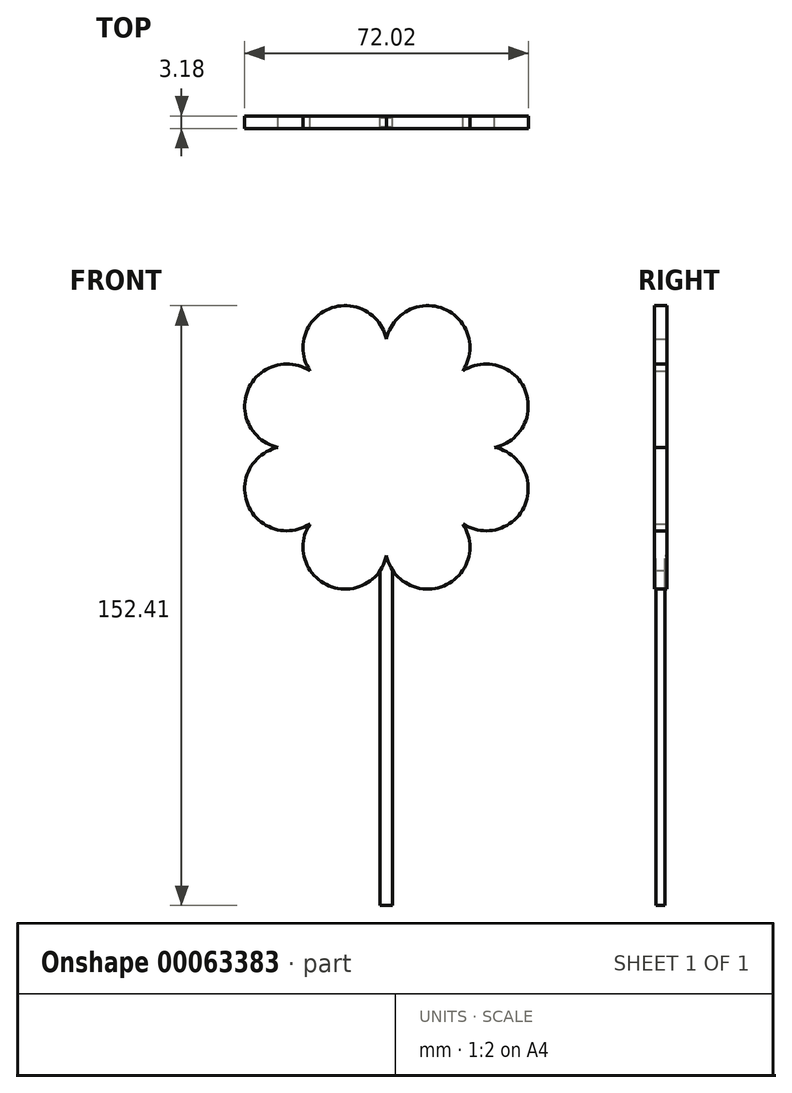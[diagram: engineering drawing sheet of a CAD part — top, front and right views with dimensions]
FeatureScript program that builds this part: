
annotation { "Feature Type Name" : "Feature", "Feature Type Description" : "" }
export const myFeature = defineFeature(function(context is Context, id is Id, definition is map)
    precondition{}
    {
        {
            var Q0;
            Q0=qCreatedBy(makeId("Front.planeOp"),FACE);
            var sketch = newSketch(context, id + "F0", { "sketchPlane" : qUnion([Q0])});
            skLineSegment(sketch, "E0", {"start": v(1.59, 0) * mm, "end": v(1.59, 88.9) * mm});
            skLineSegment(sketch, "E1", {"start": v(-1.59, 0) * mm, "end": v(-1.59, 88.9) * mm});
            skLineSegment(sketch, "E2", {"start": v(1.59, 0) * mm, "end": v(-1.59, 0) * mm});
            skCircle(sketch, "E3.cCircle", {"center": v(0, 116.4) * mm, "radius": 25.4 * mm, "construction": true});
            skLineSegment(sketch, "E3.0", {"start": v(-27.5, 116.4) * mm, "end": v(-19.44, 135.83) * mm});
            skLineSegment(sketch, "E3.1", {"start": v(-19.44, 135.83) * mm, "end": v(0, 143.89) * mm});
            skLineSegment(sketch, "E3.2", {"start": v(0, 143.89) * mm, "end": v(19.44, 135.83) * mm});
            skLineSegment(sketch, "E3.3", {"start": v(19.44, 135.83) * mm, "end": v(27.5, 116.4) * mm});
            skLineSegment(sketch, "E3.4", {"start": v(27.5, 116.4) * mm, "end": v(19.44, 96.95) * mm});
            skLineSegment(sketch, "E3.5", {"start": v(19.44, 96.95) * mm, "end": v(0, 88.9) * mm});
            skLineSegment(sketch, "E3.6", {"start": v(0, 88.9) * mm, "end": v(-19.44, 96.95) * mm});
            skLineSegment(sketch, "E3.7", {"start": v(-19.44, 96.95) * mm, "end": v(-27.5, 116.4) * mm});
            skPoint(sketch, "E3.0.midPoint", {"position": v(-23.47, 126.11) * mm});
            skLineSegment(sketch, "E4", {"start": v(1.59, 88.9) * mm, "end": v(-1.59, 88.9) * mm});
            skArc(sketch, "E5", {"start": v(-27.5, 116.4) * mm, "mid": v(-35.2, 101.81) * mm, "end": v(-19.44, 96.95) * mm});
            skArc(sketch, "E6", {"start": v(-19.44, 135.83) * mm, "mid": v(-35.2, 130.97) * mm, "end": v(-27.5, 116.4) * mm});
            skArc(sketch, "E7", {"start": v(0, 143.89) * mm, "mid": v(-14.58, 151.6) * mm, "end": v(-19.44, 135.83) * mm});
            skArc(sketch, "E8", {"start": v(19.44, 135.83) * mm, "mid": v(14.58, 151.6) * mm, "end": v(0, 143.89) * mm});
            skArc(sketch, "E9", {"start": v(27.5, 116.4) * mm, "mid": v(35.2, 130.97) * mm, "end": v(19.44, 135.83) * mm});
            skArc(sketch, "E10", {"start": v(19.44, 96.95) * mm, "mid": v(35.2, 101.81) * mm, "end": v(27.5, 116.4) * mm});
            skArc(sketch, "E11", {"start": v(0, 88.9) * mm, "mid": v(14.58, 81.2) * mm, "end": v(19.44, 96.95) * mm});
            skArc(sketch, "E12", {"start": v(-19.44, 96.95) * mm, "mid": v(-14.58, 81.2) * mm, "end": v(0, 88.9) * mm});
            skSolve(sketch);
        }
        {
            var Q0;
            Q0=makeQuery(id+"F0.imprint","IMPRINT",FACE,{"disambiguationData":[TD([[makeQuery(id+"F0.imprint","IMPRINT",EDGE,{"derivedFrom":sQuery(id+"F0.wireOp",EDGE,"E3.0")}),-1.0]])]});
            var Q1;
            {var subQ2=sQuery(id+"F0.wireOp",EDGE,"E3.5");Q1=makeQuery(id+"F0.imprint","IMPRINT",FACE,{"disambiguationData":[TD([[makeQuery(id+"F0.imprint","IMPRINT",EDGE,{"derivedFrom":subQ2}),1.0]])]});}
            var Q2;
            {var subQ0=sQuery(id+"F0.wireOp",EDGE,"E3.4");Q2=makeQuery(id+"F0.imprint","IMPRINT",FACE,{"disambiguationData":[TD([[makeQuery(id+"F0.imprint","IMPRINT",EDGE,{"derivedFrom":subQ0}),1.0]])]});}
            var Q3;
            {var subQ0=sQuery(id+"F0.wireOp",EDGE,"E3.3");Q3=makeQuery(id+"F0.imprint","IMPRINT",FACE,{"disambiguationData":[TD([[makeQuery(id+"F0.imprint","IMPRINT",EDGE,{"derivedFrom":subQ0}),1.0]])]});}
            var Q4;
            {var subQ0=sQuery(id+"F0.wireOp",EDGE,"E3.2");Q4=makeQuery(id+"F0.imprint","IMPRINT",FACE,{"disambiguationData":[TD([[makeQuery(id+"F0.imprint","IMPRINT",EDGE,{"derivedFrom":subQ0}),1.0]])]});}
            var Q5;
            {var subQ0=sQuery(id+"F0.wireOp",EDGE,"E3.1");Q5=makeQuery(id+"F0.imprint","IMPRINT",FACE,{"disambiguationData":[TD([[makeQuery(id+"F0.imprint","IMPRINT",EDGE,{"derivedFrom":subQ0}),1.0]])]});}
            var Q6;
            {var subQ0=sQuery(id+"F0.wireOp",EDGE,"E3.0");Q6=makeQuery(id+"F0.imprint","IMPRINT",FACE,{"disambiguationData":[TD([[makeQuery(id+"F0.imprint","IMPRINT",EDGE,{"derivedFrom":subQ0}),1.0]])]});}
            var Q7;
            {var subQ0=sQuery(id+"F0.wireOp",EDGE,"E3.7");Q7=makeQuery(id+"F0.imprint","IMPRINT",FACE,{"disambiguationData":[TD([[makeQuery(id+"F0.imprint","IMPRINT",EDGE,{"derivedFrom":subQ0}),1.0]])]});}
            var Q8;
            {var subQ4=sQuery(id+"F0.wireOp",EDGE,"E3.6");Q8=makeQuery(id+"F0.imprint","IMPRINT",FACE,{"disambiguationData":[TD([[makeQuery(id+"F0.imprint","IMPRINT",EDGE,{"derivedFrom":subQ4}),1.0]])]});}
            var Q9;
            {var subQ0=sQuery(id+"F0.wireOp",EDGE,"E4");var subQ1=sQuery(id+"F0.wireOp",EDGE,"E0");var subQ2=makeQuery(id+"F0.imprint","INTERSECT",VERTEX,{"derivedFrom":[subQ1,subQ0]});Q9=makeQuery(id+"F0.imprint","IMPRINT",FACE,{"disambiguationData":[TD([[makeQuery(id+"F0.imprint","IMPRINT",EDGE,{"disambiguationData":[TD([[subQ2,1.0]])],"derivedFrom":subQ1}),1.0]])]});}
            var Q10;
            {var subQ0=sQuery(id+"F0.wireOp",EDGE,"E4");var subQ1=sQuery(id+"F0.wireOp",EDGE,"E1");var subQ2=makeQuery(id+"F0.imprint","INTERSECT",VERTEX,{"derivedFrom":[subQ1,subQ0]});Q10=makeQuery(id+"F0.imprint","IMPRINT",FACE,{"disambiguationData":[TD([[makeQuery(id+"F0.imprint","IMPRINT",EDGE,{"disambiguationData":[TD([[subQ2,1.0]])],"derivedFrom":subQ1}),-1.0]])]});}
            extrude(context, id + "F1", {"entities" : qUnion([Q0, Q1, Q2, Q3, Q4, Q5, Q6, Q7, Q8, Q9, Q10]), "endBound" : BoundingType.SYMMETRIC, "depth" : 3.17 * mm});
        }
        {
            var Q0;
            {var subQ5=sQuery(id+"F0.wireOp",EDGE,"E2");Q0=makeQuery(id+"F0.imprint","IMPRINT",FACE,{"disambiguationData":[TD([[makeQuery(id+"F0.imprint","IMPRINT",EDGE,{"derivedFrom":subQ5}),-1.0]])]});}
            extrude(context, id + "F2", {"entities" : qUnion([Q0]), "operationType" : NewBodyOperationType.ADD, "endBound" : BoundingType.SYMMETRIC, "depth" : 2.38 * mm});
        }
    });
